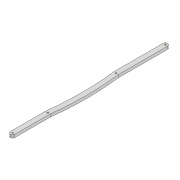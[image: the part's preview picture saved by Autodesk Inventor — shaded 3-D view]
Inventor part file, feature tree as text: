
AUTODESK INVENTOR PART (.ipt)
format: ipt  version: 2022 (Build 260153000, 153)  size: 102,400 bytes
history: native  units: mm
features: extrude x1, other x1, sketch x1
ambient origin geometry x8: Origin, YZ Plane, XZ Plane, XY Plane, X Axis, Y Axis, Z Axis, Center Point
bodies: Solid1 (feature_tree)
feature tree (3):
  extrude  "Extrusion1"  Depth=600.0mm
  other  "Work Axis3"
  sketch  "Sketch1"  dims[d0=3.3mm d1=3.3mm d2=10.0mm d3=322.934mm d4=3.3mm d5=74.182mm d6=6.0mm d7=0.0mm d8=3.3mm d9=218.733mm d12=600.0mm d13=600.0mm]
